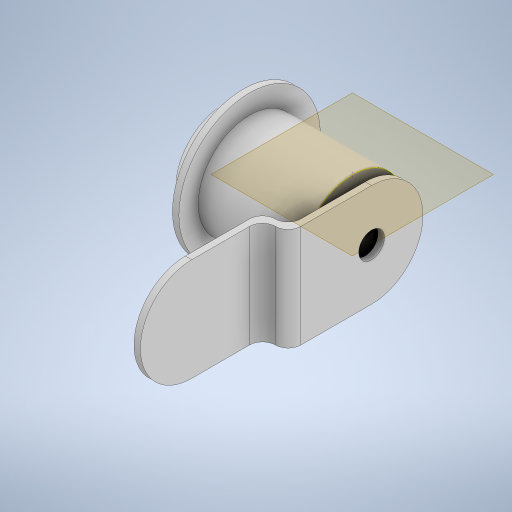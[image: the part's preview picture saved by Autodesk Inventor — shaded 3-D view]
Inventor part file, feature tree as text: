
AUTODESK INVENTOR PART (.ipt)
format: ipt  version: 2023 (Build 270158000, 158)  size: 321,024 bytes
history: native  units: mm
features: sketch x5, extrude x3, fillet x3, other x2, revolve x1
ambient origin geometry x8: Origin, YZ Plane, XZ Plane, XY Plane, X Axis, Y Axis, Z Axis, Center Point
bodies: Body1 (feature_tree)
feature tree (14):
  other  "Твердое тело1"
  revolve  "Вращение1"
  sketch  "Эскиз2"
  other  "РабПлоскость1"
  extrude  "Выдавливание1"  Depth=8.0mm
  fillet  "Сопряжение1"  Radius=16.0mm
  fillet  "Сопряжение2"  Radius=3.0mm
  fillet  "Сопряжение3"  Radius=1.0mm
  extrude  "Выдавливание2"  Depth=3.0mm
  extrude  "Выдавливание3"  Depth=7.5mm
  sketch  "Эскиз1"
  sketch  "Эскиз3"
  sketch  "Эскиз4"
  sketch  "Эскиз5"
